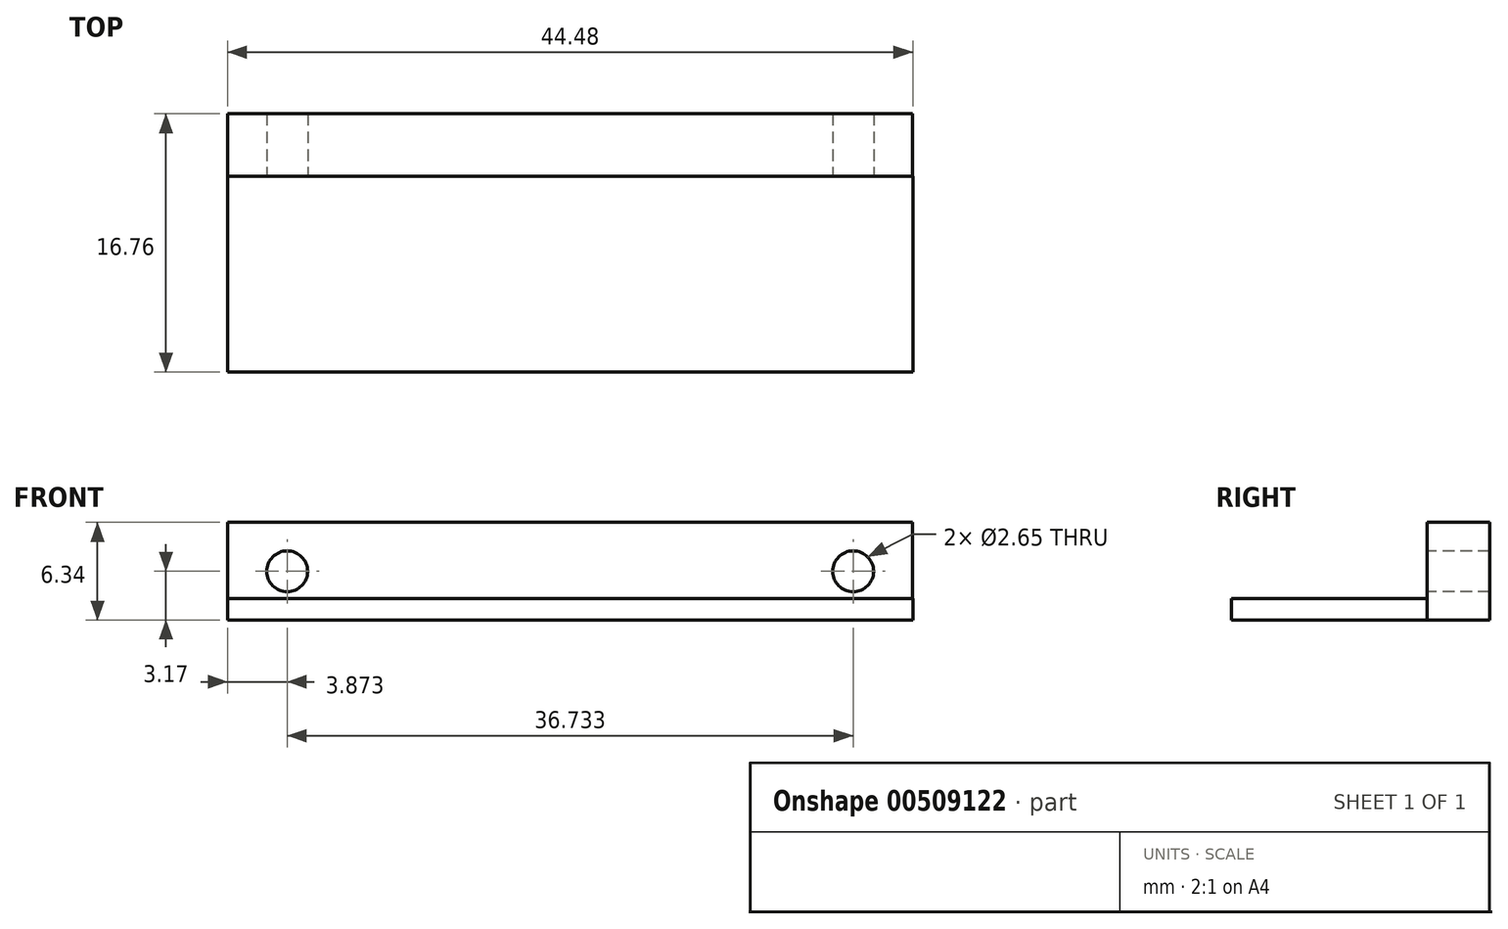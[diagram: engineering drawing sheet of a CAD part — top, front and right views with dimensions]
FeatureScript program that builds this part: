
annotation { "Feature Type Name" : "Feature", "Feature Type Description" : "" }
export const myFeature = defineFeature(function(context is Context, id is Id, definition is map)
    precondition{}
    {
        {
            var Q0;
            Q0=qCreatedBy(makeId("Front.planeOp"),FACE);
            var sketch = newSketch(context, id + "F0", { "sketchPlane" : qUnion([Q0])});
            skLineSegment(sketch, "E0.bottom", {"start": v(22.23, -3.17) * mm, "end": v(-22.23, -3.18) * mm});
            skLineSegment(sketch, "E0.top", {"start": v(22.23, 3.18) * mm, "end": v(-22.23, 3.17) * mm});
            skLineSegment(sketch, "E0.left", {"start": v(22.23, -3.17) * mm, "end": v(22.23, 3.18) * mm});
            skLineSegment(sketch, "E0.right", {"start": v(-22.23, -3.18) * mm, "end": v(-22.23, 3.17) * mm});
            skPoint(sketch, "E0.middle", {"position": v(0, 0) * mm});
            skSolve(sketch);
        }
        {
            var Q0;
            Q0 = qSketchRegion(id + "F0", true);
            extrude(context, id + "F1", {"entities" : qUnion([Q0]), "depth" : 4.06 * mm});
        }
        {
            var Q0;
            Q0=makeQuery(id+"F1.opExtrude","CAP_FACE",FACE,{"disambiguationData":[OSD([sQuery(id+"F0.wireOp",EDGE,"E0.bottom"),sQuery(id+"F0.wireOp",EDGE,"E0.top"),sQuery(id+"F0.wireOp",EDGE,"E0.left"),sQuery(id+"F0.wireOp",EDGE,"E0.right")])],"isStart":false});
            var sketch = newSketch(context, id + "F2", { "sketchPlane" : qUnion([Q0])});
            skCircle(sketch, "E1", {"center": v(-18.37, 0) * mm, "radius": 1.33 * mm});
            skSolve(sketch);
        }
        {
            var Q0;
            Q0=makeQuery(id+"F2.imprint","IMPRINT",FACE,{"disambiguationData":[TD([[makeQuery(id+"F2.imprint","IMPRINT",EDGE,{"derivedFrom":sQuery(id+"F2.wireOp",EDGE,"E1")}),1.0]])]});
            extrude(context, id + "F3", {"entities" : qUnion([Q0]), "operationType" : NewBodyOperationType.REMOVE, "oppositeDirection" : true, "depth" : 25.4 * mm});
        }
        {
            var Q0;
            Q0=makeQuery(id+"F1.opExtrude","CAP_FACE",FACE,{"disambiguationData":[OSD([sQuery(id+"F0.wireOp",EDGE,"E0.bottom"),sQuery(id+"F0.wireOp",EDGE,"E0.top"),sQuery(id+"F0.wireOp",EDGE,"E0.left"),sQuery(id+"F0.wireOp",EDGE,"E0.right")])],"isStart":false});
            var sketch = newSketch(context, id + "F4", { "sketchPlane" : qUnion([Q0])});
            skLineSegment(sketch, "E2", {"start": v(0, 9.94) * mm, "end": v(0, -8.43) * mm, "construction": true});
            skPoint(sketch, "E2.startSnap0", {"position": v(0, 3.18) * mm});
            skPoint(sketch, "E2.endSnap0", {"position": v(0, -3.18) * mm});
            skSolve(sketch);
        }
        {
            var Q0;
            Q0=makeQuery(id+"F2.imprint","IMPRINT",FACE,{"disambiguationData":[TD([[makeQuery(id+"F2.imprint","IMPRINT",EDGE,{"derivedFrom":sQuery(id+"F2.wireOp",EDGE,"E1")}),1.0]])]});
            extrude(context, id + "F5", {"entities" : qUnion([Q0]), "operationType" : NewBodyOperationType.REMOVE, "oppositeDirection" : true, "depth" : 25.4 * mm});
        }
        {
            var Q0;
            Q0=makeQuery(id+"F1.opExtrude","SWEPT_BODY",BODY,{"disambiguationData":[OSD([sQuery(id+"F0.wireOp",EDGE,"E0.bottom"),sQuery(id+"F0.wireOp",EDGE,"E0.top"),sQuery(id+"F0.wireOp",EDGE,"E0.left"),sQuery(id+"F0.wireOp",EDGE,"E0.right")])]});
            var Q1;
            Q1=qCreatedBy(makeId("Right.planeOp"),FACE);
            mirror(context, id + "F6", {"operationType" : NewBodyOperationType.INTERSECT, "entities" : qUnion([Q0]), "mirrorPlane" : qUnion([Q1])});
        }
        {
            var Q0;
            Q0=makeQuery(id+"F4.imprint","IMPRINT",FACE,{"disambiguationData":[TD([[makeQuery(id+"F4.imprint","IMPRINT",EDGE,{"derivedFrom":makeQuery(id+"F1.opExtrude","CAP_EDGE",EDGE,{"disambiguationData":[OSD([sQuery(id+"F0.wireOp",EDGE,"E0.bottom")])],"isStart":false})}),-1.0]])]});
            var sketch = newSketch(context, id + "F7", { "sketchPlane" : qUnion([Q0])});
            skLineSegment(sketch, "E3.bottom", {"start": v(22.24, -3.16) * mm, "end": v(-22.24, -3.16) * mm});
            skLineSegment(sketch, "E3.top", {"start": v(22.24, -1.76) * mm, "end": v(-22.24, -1.76) * mm});
            skLineSegment(sketch, "E3.left", {"start": v(22.24, -3.16) * mm, "end": v(22.24, -1.76) * mm});
            skLineSegment(sketch, "E3.right", {"start": v(-22.24, -3.16) * mm, "end": v(-22.24, -1.76) * mm});
            skPoint(sketch, "E3.middle", {"position": v(0, -2.46) * mm});
            skSolve(sketch);
        }
        {
            var Q0;
            Q0 = qSketchRegion(id + "F7", true);
            extrude(context, id + "F8", {"entities" : qUnion([Q0]), "operationType" : NewBodyOperationType.ADD, "depth" : 12.7 * mm});
        }
    });
